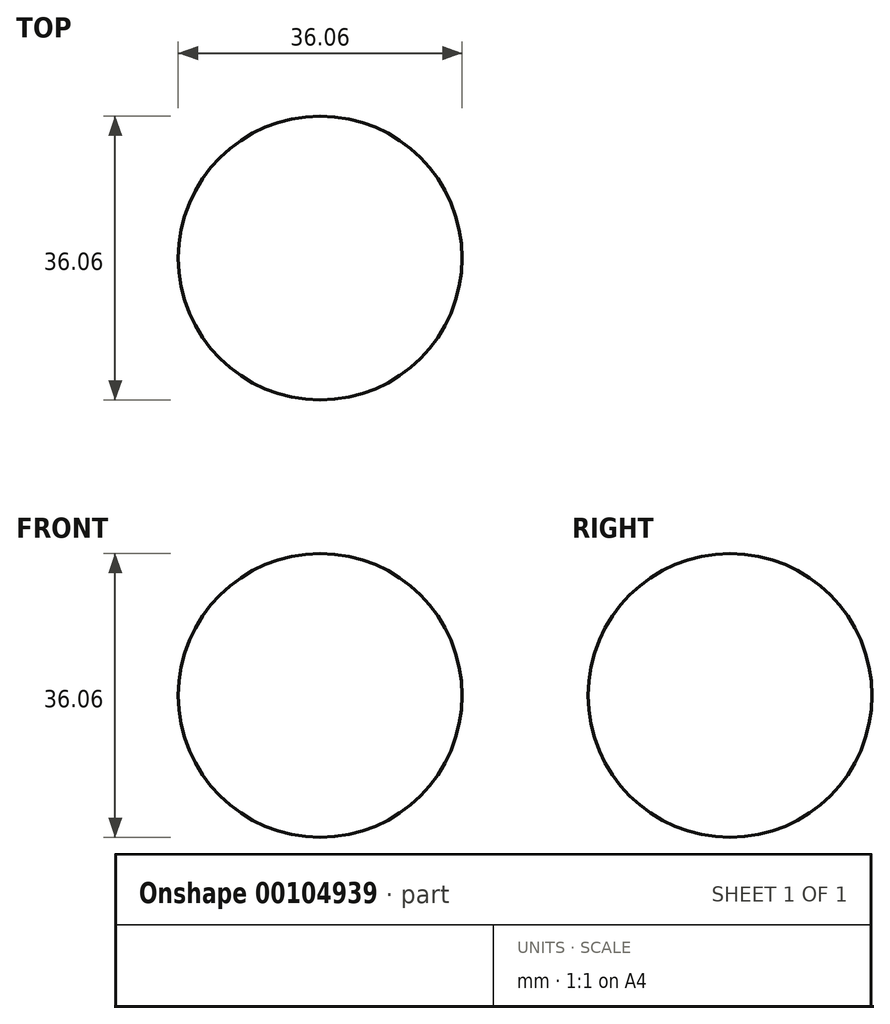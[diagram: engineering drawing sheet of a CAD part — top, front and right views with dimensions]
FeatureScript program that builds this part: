
annotation { "Feature Type Name" : "Feature", "Feature Type Description" : "" }
export const myFeature = defineFeature(function(context is Context, id is Id, definition is map)
    precondition{}
    {
        {
            var Q0;
            Q0=qCreatedBy(makeId("Front.planeOp"),FACE);
            var sketch = newSketch(context, id + "F0", { "sketchPlane" : qUnion([Q0])});
            skArc(sketch, "E0", {"start": v(0, 18.03) * mm, "mid": v(-18.03, 0) * mm, "end": v(0, -18.03) * mm});
            skLineSegment(sketch, "E1", {"start": v(0, 18.03) * mm, "end": v(0, -18.03) * mm});
            skSolve(sketch);
        }
        {
            var Q0;
            Q0 = qSketchRegion(id + "F0", true);
            var Q1;
            Q1=sQuery(id+"F0.wireOp",EDGE,"E1");
            revolve(context, id + "F1", {"entities" : qUnion([Q0]), "axis" : qUnion([Q1]), "revolveType" : RevolveType.ONE_DIRECTION, "angle" : 360 * degree});
        }
    });
